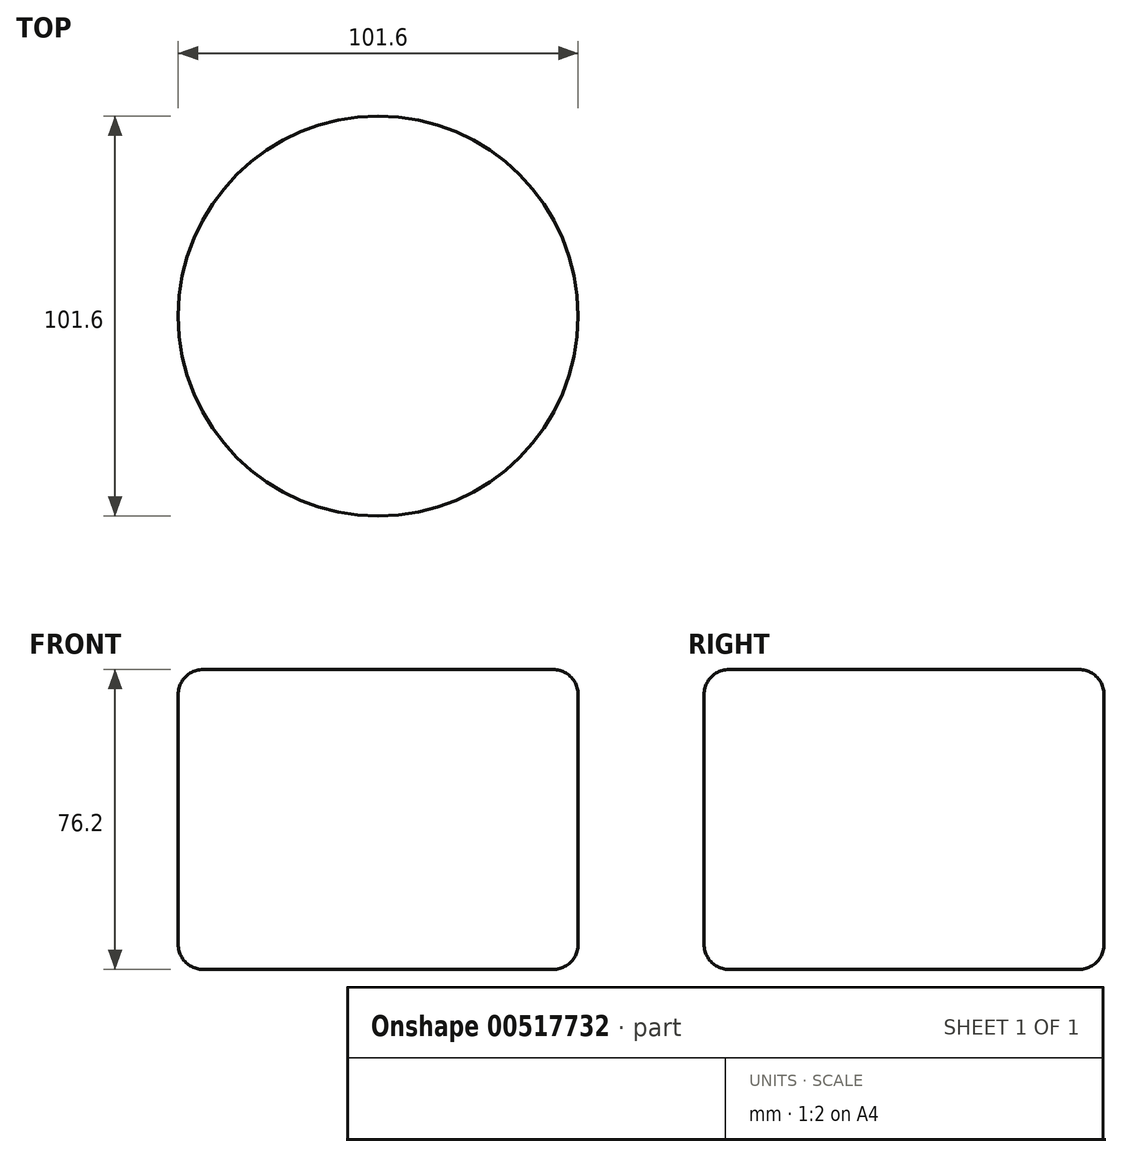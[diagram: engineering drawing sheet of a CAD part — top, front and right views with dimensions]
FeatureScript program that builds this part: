
annotation { "Feature Type Name" : "Feature", "Feature Type Description" : "" }
export const myFeature = defineFeature(function(context is Context, id is Id, definition is map)
    precondition{}
    {
        {
            var Q0;
            Q0=qCreatedBy(makeId("Front.planeOp"),FACE);
            var sketch = newSketch(context, id + "F0", { "sketchPlane" : qUnion([Q0])});
            skLineSegment(sketch, "E0.bottom", {"start": v(19.05, 38.1) * mm, "end": v(-19.05, 38.1) * mm});
            skLineSegment(sketch, "E0.top", {"start": v(19.05, -38.1) * mm, "end": v(-19.05, -38.1) * mm});
            skLineSegment(sketch, "E0.left", {"start": v(25.4, 31.75) * mm, "end": v(25.4, -31.75) * mm});
            skLineSegment(sketch, "E0.right", {"start": v(-25.4, 31.75) * mm, "end": v(-25.4, -31.75) * mm});
            skPoint(sketch, "E0.middle", {"position": v(0, 0) * mm});
            skPoint(sketch, "E1.visualSharp", {"position": v(-25.4, 38.1) * mm});
            skArc(sketch, "E1.filletArc", {"start": v(-19.05, 38.1) * mm, "mid": v(-23.54, 36.24) * mm, "end": v(-25.4, 31.75) * mm});
            skPoint(sketch, "E2.visualSharp", {"position": v(25.4, 38.1) * mm});
            skArc(sketch, "E2.filletArc", {"start": v(25.4, 31.75) * mm, "mid": v(23.54, 36.24) * mm, "end": v(19.05, 38.1) * mm});
            skPoint(sketch, "E3.visualSharp", {"position": v(25.4, -38.1) * mm});
            skArc(sketch, "E3.filletArc", {"start": v(19.05, -38.1) * mm, "mid": v(23.54, -36.24) * mm, "end": v(25.4, -31.75) * mm});
            skPoint(sketch, "E4.visualSharp", {"position": v(-25.4, -38.1) * mm});
            skArc(sketch, "E4.filletArc", {"start": v(-25.4, -31.75) * mm, "mid": v(-23.54, -36.24) * mm, "end": v(-19.05, -38.1) * mm});
            skSolve(sketch);
        }
        {
            var Q0;
            Q0=makeQuery(id+"F0.imprint","IMPRINT",FACE,{"disambiguationData":[TD([[makeQuery(id+"F0.imprint","IMPRINT",EDGE,{"derivedFrom":sQuery(id+"F0.wireOp",EDGE,"E0.bottom")}),1.0]])]});
            var Q1;
            Q1=sQuery(id+"F0.wireOp",EDGE,"E0.right");
            revolve(context, id + "F1", {"entities" : qUnion([Q0]), "axis" : qUnion([Q1]), "revolveType" : RevolveType.FULL});
        }
    });
